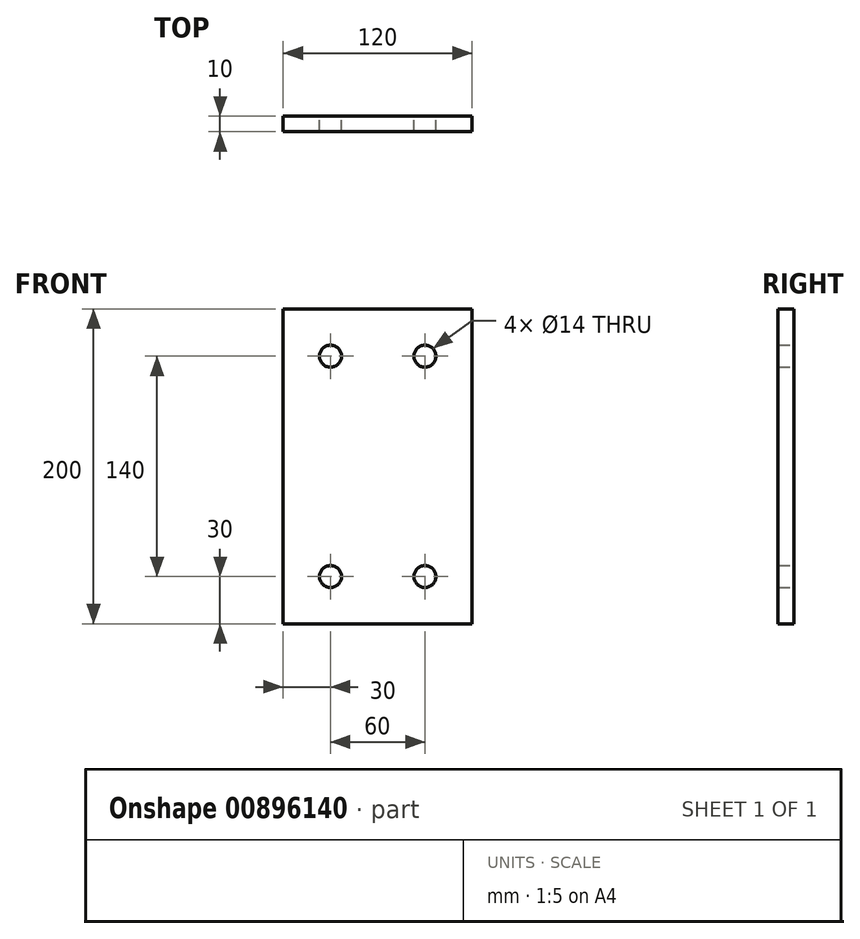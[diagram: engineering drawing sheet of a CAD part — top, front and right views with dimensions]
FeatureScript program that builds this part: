
annotation { "Feature Type Name" : "Feature", "Feature Type Description" : "" }
export const myFeature = defineFeature(function(context is Context, id is Id, definition is map)
    precondition{}
    {
        {
            var Q0;
            Q0=qCreatedBy(makeId("Front.planeOp"),FACE);
            var sketch = newSketch(context, id + "F0", { "sketchPlane" : qUnion([Q0])});
            skLineSegment(sketch, "E0.bottom", {"start": v(60, 100) * mm, "end": v(-60, 100) * mm});
            skLineSegment(sketch, "E0.top", {"start": v(60, -100) * mm, "end": v(-60, -100) * mm});
            skLineSegment(sketch, "E0.left", {"start": v(60, 100) * mm, "end": v(60, -100) * mm});
            skLineSegment(sketch, "E0.right", {"start": v(-60, 100) * mm, "end": v(-60, -100) * mm});
            skPoint(sketch, "E0.middle", {"position": v(0, 0) * mm});
            skCircle(sketch, "E1", {"center": v(-30, 70) * mm, "radius": 7 * mm});
            skCircle(sketch, "E2", {"center": v(30, 70) * mm, "radius": 7 * mm});
            skCircle(sketch, "E3", {"center": v(-30, -70) * mm, "radius": 7 * mm});
            skCircle(sketch, "E4", {"center": v(30, -70) * mm, "radius": 7 * mm});
            skSolve(sketch);
        }
        {
            var Q0;
            Q0=makeQuery(id+"F0.imprint","IMPRINT",FACE,{"disambiguationData":[TD([[makeQuery(id+"F0.imprint","IMPRINT",EDGE,{"derivedFrom":sQuery(id+"F0.wireOp",EDGE,"E0.bottom")}),1.0]])]});
            var Q1;
            Q1=makeQuery(id+"F0.imprint","IMPRINT",FACE,{"disambiguationData":[TD([[makeQuery(id+"F0.imprint","IMPRINT",EDGE,{"derivedFrom":sQuery(id+"F0.wireOp",EDGE,"IxA8HR9I-vB6L-gbE1-t8Bs-stX18FFaMMz4.bottom")}),1.0]])]});
            extrude(context, id + "F1", {"entities" : qUnion([Q0, Q1]), "depth" : 10 * mm, "offsetDistance" : 25 * mm});
        }
    });
